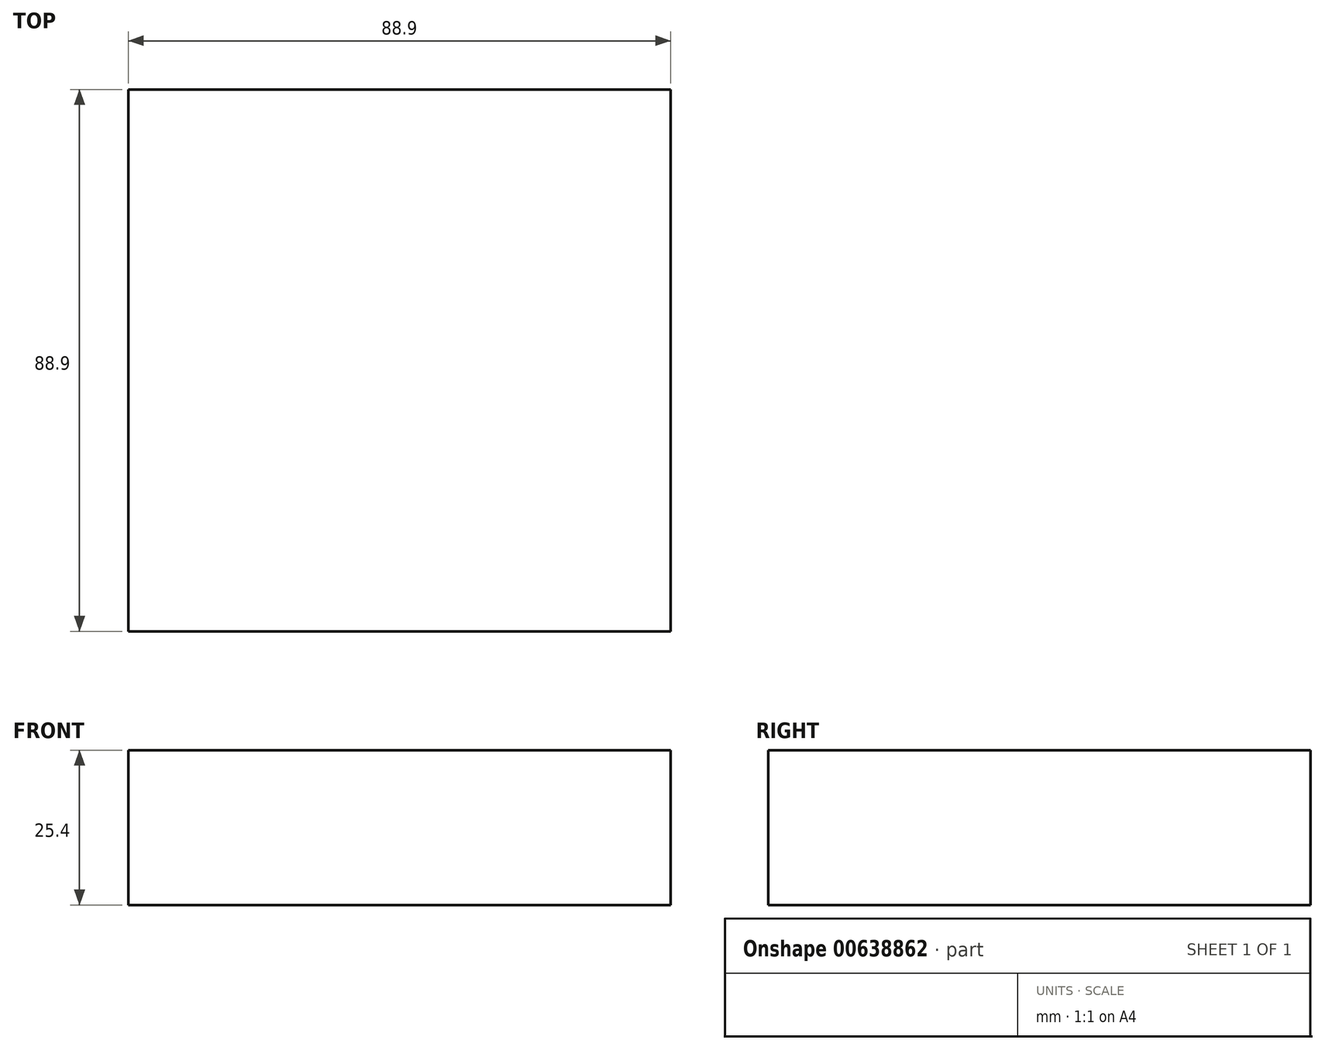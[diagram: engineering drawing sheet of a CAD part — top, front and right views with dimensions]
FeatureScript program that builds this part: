
annotation { "Feature Type Name" : "Feature", "Feature Type Description" : "" }
export const myFeature = defineFeature(function(context is Context, id is Id, definition is map)
    precondition{}
    {
        {
            var Q0;
            Q0=qCreatedBy(makeId("Top.planeOp"),FACE);
            var sketch = newSketch(context, id + "F0", { "sketchPlane" : qUnion([Q0])});
            skLineSegment(sketch, "E0.bottom", {"start": v(44.45, 44.45) * mm, "end": v(-44.45, 44.45) * mm});
            skLineSegment(sketch, "E0.top", {"start": v(44.45, -44.45) * mm, "end": v(-44.45, -44.45) * mm});
            skLineSegment(sketch, "E0.left", {"start": v(44.45, 44.45) * mm, "end": v(44.45, -44.45) * mm});
            skLineSegment(sketch, "E0.right", {"start": v(-44.45, 44.45) * mm, "end": v(-44.45, -44.45) * mm});
            skPoint(sketch, "E0.middle", {"position": v(0, 0) * mm});
            skSolve(sketch);
        }
        {
            var Q0;
            Q0 = qSketchRegion(id + "F0", true);
            extrude(context, id + "F1", {"entities" : qUnion([Q0]), "depth" : 25.4 * mm, "offsetDistance" : 25.4 * mm});
        }
    });
